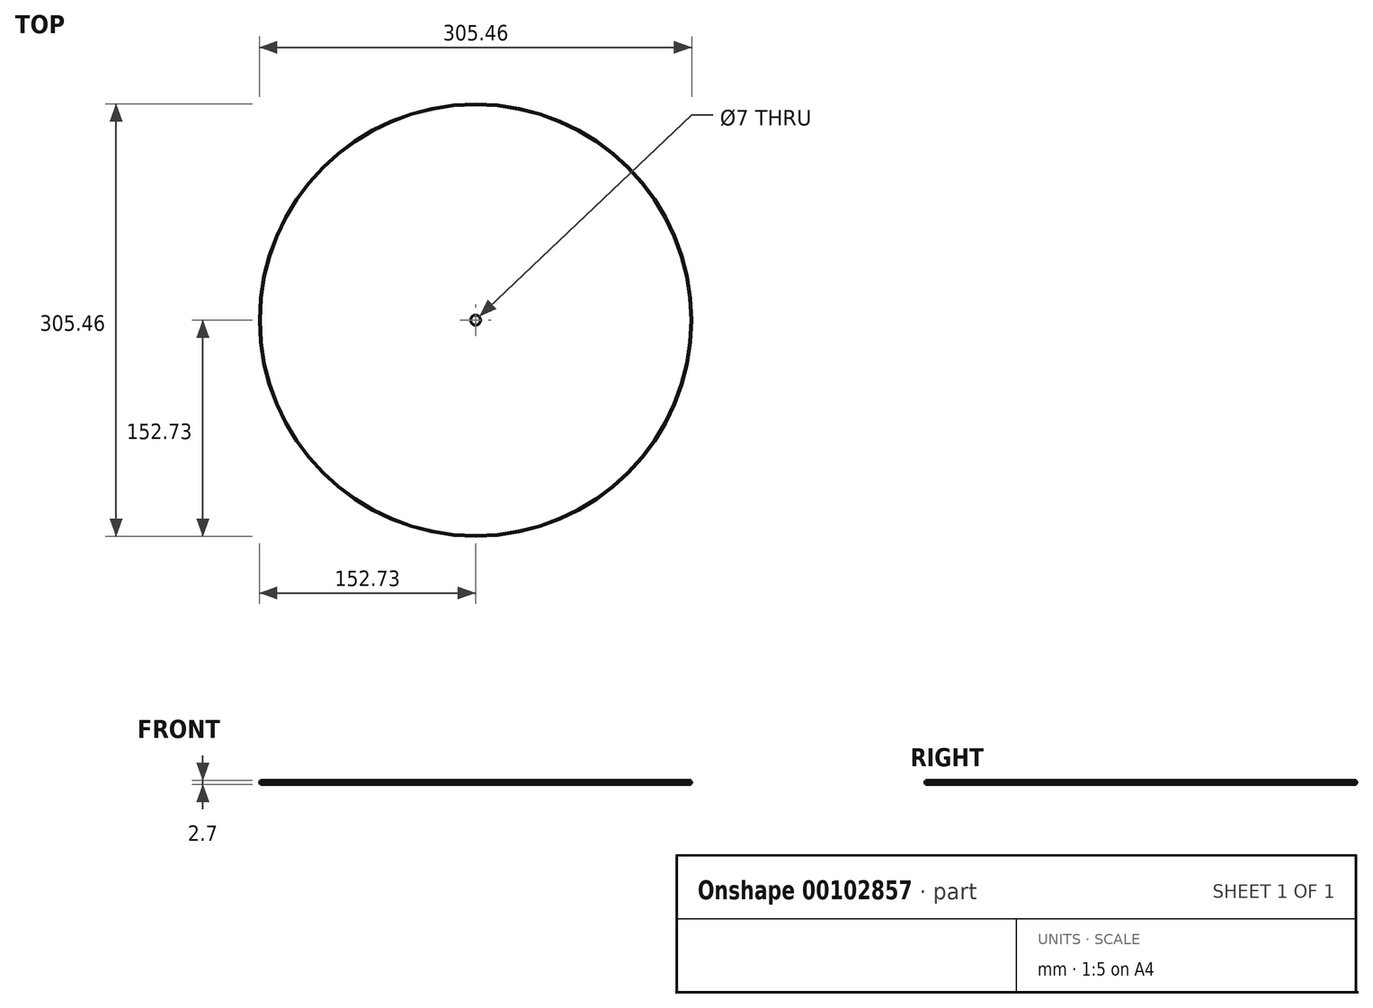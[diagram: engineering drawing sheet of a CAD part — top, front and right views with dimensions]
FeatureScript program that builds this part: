
annotation { "Feature Type Name" : "Feature", "Feature Type Description" : "" }
export const myFeature = defineFeature(function(context is Context, id is Id, definition is map)
    precondition{}
    {
        {
            var Q0;
            Q0=qCreatedBy(makeId("Front.planeOp"),FACE);
            var sketch = newSketch(context, id + "F0", { "sketchPlane" : qUnion([Q0])});
            skLineSegment(sketch, "E0", {"start": v(-152.1, 6.54) * mm, "end": v(-20.18, 6.54) * mm});
            skLineSegment(sketch, "E1", {"start": v(0, 30.8) * mm, "end": v(0, -118.37) * mm});
            skLineSegment(sketch, "E2", {"start": v(-19.86, 6.42) * mm, "end": v(-12, -0.13) * mm});
            skLineSegment(sketch, "E3.0", {"start": v(-154.43, 7.69) * mm, "end": v(-152.73, 7.69) * mm});
            skLineSegment(sketch, "E4", {"start": v(-154.66, 7.61) * mm, "end": v(-164.14, 0.74) * mm});
            skPoint(sketch, "E5.visualSharp", {"position": v(-152.9, 6.54) * mm});
            skArc(sketch, "E5.filletArc", {"start": v(-152.4, 6.79) * mm, "mid": v(-152.3, 6.6) * mm, "end": v(-152.1, 6.54) * mm});
            skLineSegment(sketch, "E6", {"start": v(-152.53, 7.52) * mm, "end": v(-152.4, 6.79) * mm});
            skPoint(sketch, "E7.visualSharp", {"position": v(-152.56, 7.69) * mm});
            skArc(sketch, "E7.filletArc", {"start": v(-152.53, 7.52) * mm, "mid": v(-152.6, 7.64) * mm, "end": v(-152.73, 7.69) * mm});
            skPoint(sketch, "E8.visualSharp", {"position": v(-154.56, 7.69) * mm});
            skArc(sketch, "E8.filletArc", {"start": v(-154.43, 7.69) * mm, "mid": v(-154.55, 7.67) * mm, "end": v(-154.66, 7.61) * mm});
            skPoint(sketch, "E9.visualSharp", {"position": v(-20, 6.54) * mm});
            skArc(sketch, "E9.filletArc", {"start": v(-19.86, 6.42) * mm, "mid": v(-20.01, 6.5) * mm, "end": v(-20.18, 6.54) * mm});
            skLineSegment(sketch, "E10", {"start": v(-164.17, -4.7) * mm, "end": v(-194.17, -4.7) * mm});
            skLineSegment(sketch, "E11.0", {"start": v(-10, -0.13) * mm, "end": v(-10, -32.31) * mm});
            skLineSegment(sketch, "E12.0", {"start": v(-194.17, -4.7) * mm, "end": v(-194.17, -32.31) * mm});
            skPoint(sketch, "E13.endSnap0", {"position": v(-154.55, 7.67) * mm});
            skLineSegment(sketch, "E14.0", {"start": v(-164.14, 0.74) * mm, "end": v(-164.17, -4.7) * mm});
            skLineSegment(sketch, "E15.0", {"start": v(-194.17, -32.31) * mm, "end": v(-10, -32.31) * mm});
            skPoint(sketch, "E16.orphan", {"position": v(-194.17, -4.7) * mm});
            skPoint(sketch, "E17.orphan", {"position": v(-194.17, 7.31) * mm});
            skLineSegment(sketch, "E18.0", {"start": v(-154.84, 7.86) * mm, "end": v(-164.14, 1.11) * mm});
            skLineSegment(sketch, "E19.0", {"start": v(-152.1, 6.84) * mm, "end": v(-20.18, 6.84) * mm});
            skArc(sketch, "E20.0", {"start": v(-154.43, 7.99) * mm, "mid": v(-154.64, 7.95) * mm, "end": v(-154.84, 7.86) * mm});
            skLineSegment(sketch, "E21.0", {"start": v(-154.43, 7.99) * mm, "end": v(-152.73, 7.99) * mm});
            skLineSegment(sketch, "E22.0", {"start": v(-152.23, 7.57) * mm, "end": v(-152.1, 6.84) * mm});
            skArc(sketch, "E23.0", {"start": v(-152.23, 7.57) * mm, "mid": v(-152.4, 7.87) * mm, "end": v(-152.73, 7.99) * mm});
            skPoint(sketch, "E24.orphan", {"position": v(0, -33.1) * mm});
            skLineSegment(sketch, "E25", {"start": v(-12, -0.13) * mm, "end": v(-10, -0.13) * mm});
            skLineSegment(sketch, "E26.0", {"start": v(-19.67, 6.65) * mm, "end": v(-11.8, 0.1) * mm});
            skArc(sketch, "E27.0", {"start": v(-19.67, 6.65) * mm, "mid": v(-19.9, 6.8) * mm, "end": v(-20.18, 6.84) * mm});
            skPoint(sketch, "E28.orphan", {"position": v(-194.17, -56.66) * mm});
            skLineSegment(sketch, "E29.0", {"start": v(-175.89, 8.19) * mm, "end": v(-152.8, 8.19) * mm, "construction": true});
            skArc(sketch, "E30.MirrorCS", {"start": v(-19.86, 9.95) * mm, "mid": v(-20.01, 9.87) * mm, "end": v(-20.18, 9.84) * mm});
            skArc(sketch, "E31.MirrorCS", {"start": v(-19.67, 9.72) * mm, "mid": v(-19.9, 9.59) * mm, "end": v(-20.18, 9.54) * mm});
            skLineSegment(sketch, "E32.MirrorCS", {"start": v(-19.86, 9.95) * mm, "end": v(-12, 16.5) * mm});
            skLineSegment(sketch, "E33.MirrorCS", {"start": v(-19.67, 9.72) * mm, "end": v(-11.8, 16.27) * mm});
            skLineSegment(sketch, "E34.MirrorCS", {"start": v(-12, 16.5) * mm, "end": v(-10, 16.5) * mm});
            skPoint(sketch, "E35.MirrorP", {"position": v(-20, 9.84) * mm});
            skLineSegment(sketch, "E36.MirrorCS", {"start": v(-194.17, 48.69) * mm, "end": v(-10, 48.69) * mm});
            skLineSegment(sketch, "E37.MirrorCS", {"start": v(-152.1, 9.54) * mm, "end": v(-20.18, 9.54) * mm});
            skLineSegment(sketch, "E38.MirrorCS", {"start": v(-10, 16.5) * mm, "end": v(-10, 48.69) * mm});
            skLineSegment(sketch, "E39.MirrorCS", {"start": v(-152.1, 9.84) * mm, "end": v(-20.18, 9.84) * mm});
            skPoint(sketch, "E40.MirrorP", {"position": v(0, 49.48) * mm});
            skLineSegment(sketch, "E41.MirrorCS", {"start": v(-152.23, 8.8) * mm, "end": v(-152.1, 9.54) * mm});
            skLineSegment(sketch, "E42.MirrorCS", {"start": v(-154.43, 8.69) * mm, "end": v(-152.73, 8.69) * mm});
            skArc(sketch, "E43.MirrorCS", {"start": v(-152.23, 8.8) * mm, "mid": v(-152.4, 8.5) * mm, "end": v(-152.73, 8.39) * mm});
            skArc(sketch, "E44.MirrorCS", {"start": v(-152.4, 9.6) * mm, "mid": v(-152.3, 9.77) * mm, "end": v(-152.1, 9.84) * mm});
            skArc(sketch, "E45.MirrorCS", {"start": v(-154.43, 8.69) * mm, "mid": v(-154.55, 8.7) * mm, "end": v(-154.66, 8.76) * mm});
            skLineSegment(sketch, "E46.MirrorCS", {"start": v(-152.53, 8.85) * mm, "end": v(-152.4, 9.6) * mm});
            skArc(sketch, "E47.MirrorCS", {"start": v(-154.43, 8.39) * mm, "mid": v(-154.64, 8.42) * mm, "end": v(-154.84, 8.52) * mm});
            skArc(sketch, "E48.MirrorCS", {"start": v(-152.53, 8.85) * mm, "mid": v(-152.6, 8.74) * mm, "end": v(-152.73, 8.69) * mm});
            skLineSegment(sketch, "E49.MirrorCS", {"start": v(-154.43, 8.39) * mm, "end": v(-152.73, 8.39) * mm});
            skLineSegment(sketch, "E50.MirrorCS", {"start": v(-154.84, 8.52) * mm, "end": v(-164.14, 15.27) * mm});
            skLineSegment(sketch, "E51.MirrorCS", {"start": v(-164.14, 15.64) * mm, "end": v(-164.17, 21.08) * mm});
            skLineSegment(sketch, "E52.MirrorCS", {"start": v(-154.66, 8.76) * mm, "end": v(-164.14, 15.64) * mm});
            skPoint(sketch, "E53.MirrorP", {"position": v(-154.56, 8.69) * mm});
            skPoint(sketch, "E54.MirrorP", {"position": v(-194.17, 9.06) * mm});
            skPoint(sketch, "E55.MirrorP", {"position": v(-154.55, 8.7) * mm});
            skLineSegment(sketch, "E56.MirrorCS", {"start": v(-152.1, 9.54) * mm, "end": v(-20.3, 9.54) * mm});
            skPoint(sketch, "E57.MirrorP", {"position": v(-152.9, 9.84) * mm});
            skPoint(sketch, "E58.MirrorP", {"position": v(-194.17, 73.04) * mm});
            skLineSegment(sketch, "E59.MirrorCS", {"start": v(-164.17, 21.08) * mm, "end": v(-194.17, 21.08) * mm});
            skLineSegment(sketch, "E60.MirrorCS", {"start": v(-194.17, 21.08) * mm, "end": v(-194.17, 48.69) * mm});
            skLineSegment(sketch, "E61.MirrorCS", {"start": v(-152.1, 6.84) * mm, "end": v(-20.3, 6.84) * mm});
            skPoint(sketch, "E62.MirrorP", {"position": v(-194.17, 21.09) * mm});
            skPoint(sketch, "E63.MirrorP", {"position": v(-152.56, 8.69) * mm});
            skPoint(sketch, "E64.orphan", {"position": v(-152.31, 8.35) * mm});
            skPoint(sketch, "E65.orphan", {"position": v(-152.31, 8.02) * mm});
            skLineSegment(sketch, "E66", {"start": v(-152.73, 8.39) * mm, "end": v(-152.73, 7.99) * mm});
            skPoint(sketch, "E67.orphan", {"position": v(-20.3, 9.54) * mm});
            skPoint(sketch, "E68.orphan", {"position": v(-20.3, 6.84) * mm});
            skLineSegment(sketch, "E69", {"start": v(-20.18, 9.54) * mm, "end": v(-3.5, 9.54) * mm});
            skLineSegment(sketch, "E70", {"start": v(-20.18, 6.84) * mm, "end": v(-3.5, 6.84) * mm});
            skLineSegment(sketch, "E71.0", {"start": v(-15.3, 2.62) * mm, "end": v(-14.83, 2.62) * mm});
            skLineSegment(sketch, "E72", {"start": v(-3.5, 9.54) * mm, "end": v(-3.5, -32.31) * mm});
            skLineSegment(sketch, "E73", {"start": v(-10, -32.31) * mm, "end": v(-3.5, -32.31) * mm});
            skPoint(sketch, "E74.end.orphan", {"position": v(-3.5, 0) * mm});
            skLineSegment(sketch, "E75", {"start": v(-11.8, 0.1) * mm, "end": v(-3.5, 0.1) * mm});
            skLineSegment(sketch, "E76", {"start": v(-6.66, 8.19) * mm, "end": v(14.92, 8.19) * mm, "construction": true});
            skArc(sketch, "E77.MirrorCS", {"start": v(-19.67, 7.02) * mm, "mid": v(-19.9, 6.89) * mm, "end": v(-20.18, 6.84) * mm});
            skLineSegment(sketch, "E78.MirrorCS", {"start": v(-11.8, 16.27) * mm, "end": v(-3.5, 16.27) * mm});
            skLineSegment(sketch, "E79.MirrorCS", {"start": v(-10, 48.69) * mm, "end": v(-3.5, 48.69) * mm});
            skLineSegment(sketch, "E80.MirrorCS", {"start": v(-3.5, 6.84) * mm, "end": v(-3.5, 48.69) * mm});
            skLineSegment(sketch, "E81", {"start": v(-3.5, 48.69) * mm, "end": v(-3.5, 9.54) * mm});
            skPoint(sketch, "E82.orphan", {"position": v(-10, 16.5) * mm});
            skLineSegment(sketch, "E83", {"start": v(-164.14, 15.64) * mm, "end": v(-164.14, 15.27) * mm});
            skLineSegment(sketch, "E84", {"start": v(-164.14, 0.74) * mm, "end": v(-164.14, 1.11) * mm});
            skSolve(sketch);
        }
        {
            var Q0;
            Q0=makeQuery(id+"F0.imprint","IMPRINT",FACE,{"disambiguationData":[TD([[makeQuery(id+"F0.imprint","IMPRINT",EDGE,{"derivedFrom":sQuery(id+"F0.wireOp",EDGE,"E19.0")}),1.0]])]});
            var Q1;
            Q1=sQuery(id+"F0.wireOp",EDGE,"E1");
            revolve(context, id + "F1", {"entities" : qUnion([Q0]), "axis" : qUnion([Q1]), "revolveType" : RevolveType.FULL});
        }
    });
